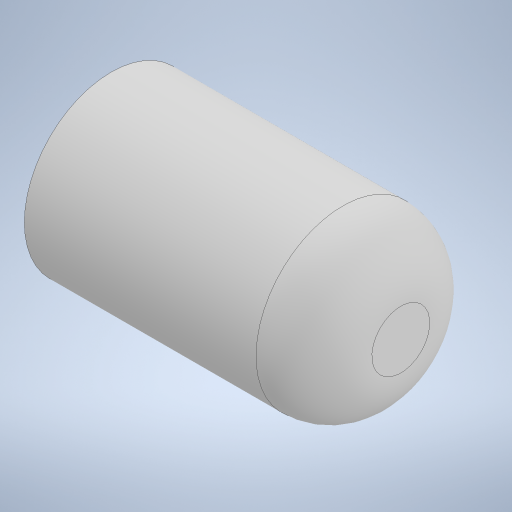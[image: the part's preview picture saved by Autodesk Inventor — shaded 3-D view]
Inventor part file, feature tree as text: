
AUTODESK INVENTOR PART (.ipt)
format: ipt  version: 2023 (Build 270158000, 158)  size: 221,184 bytes
history: native  units: in
note: dims shown in document units (in); Inventor stores cm internally (conversion verified against a paired STEP export)
features: sketch x2, extrude x1, fillet x1
ambient origin geometry x8: Origin, YZ Plane, XZ Plane, XY Plane, X Axis, Y Axis, Z Axis, Center Point
bodies: Solid1 (feature_tree)
feature tree (4):
  sketch  "Sketch1"  dims[d0=0.2362in d1=0.3937in d2=0.0in]
  extrude  "Extrusion1"  Depth=0.3937in TaperAngle=0.0deg
  fillet  "Face Fillet1"
  sketch  "Sketch2"  dims[d3=0.0787in]
